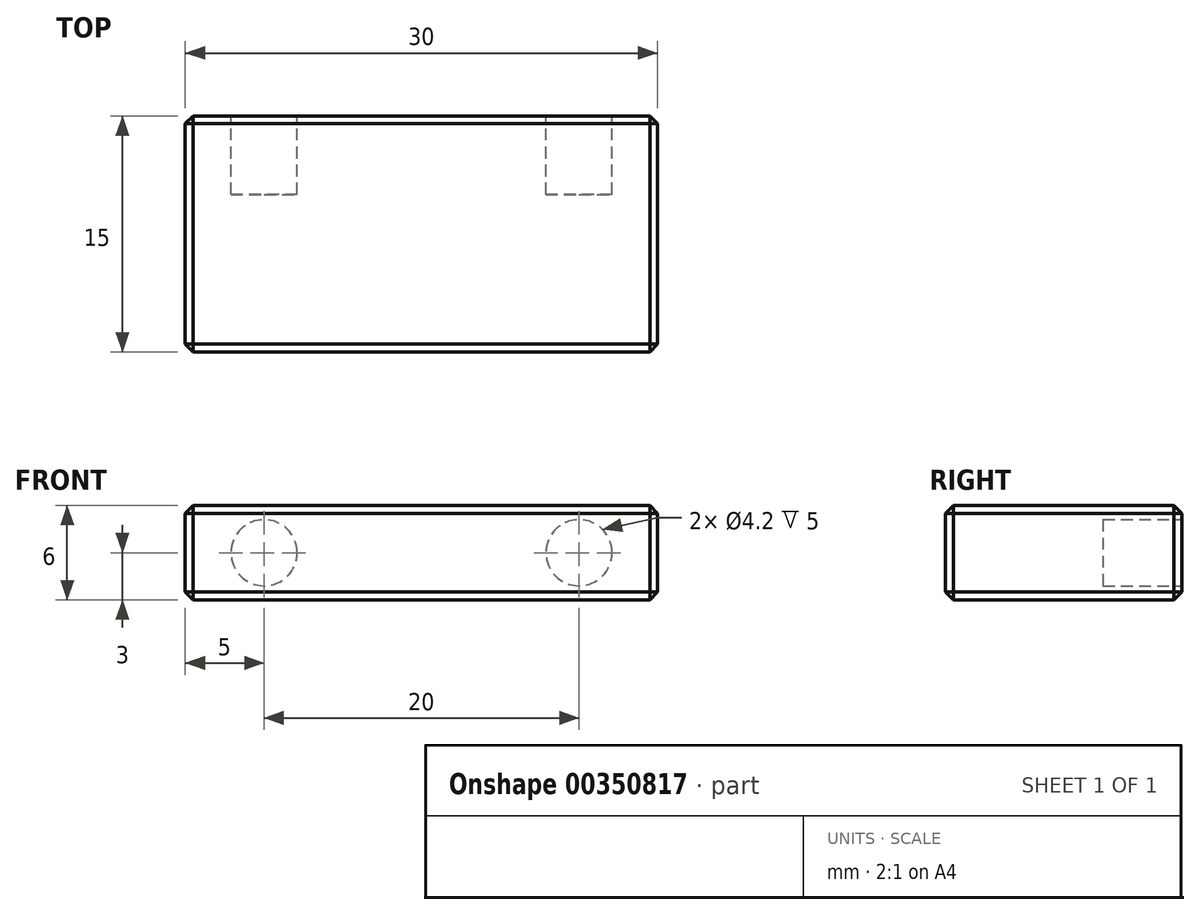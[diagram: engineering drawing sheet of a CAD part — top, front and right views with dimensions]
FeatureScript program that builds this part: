
annotation { "Feature Type Name" : "Feature", "Feature Type Description" : "" }
export const myFeature = defineFeature(function(context is Context, id is Id, definition is map)
    precondition{}
    {
        {
            var Q0;
            Q0=qCreatedBy(makeId("Front.planeOp"),FACE);
            var sketch = newSketch(context, id + "F0", { "sketchPlane" : qUnion([Q0])});
            skLineSegment(sketch, "E0.bottom", {"start": v(15, -3) * mm, "end": v(-15, -3) * mm});
            skLineSegment(sketch, "E0.top", {"start": v(15, 3) * mm, "end": v(-15, 3) * mm});
            skLineSegment(sketch, "E0.left", {"start": v(15, -3) * mm, "end": v(15, 3) * mm});
            skLineSegment(sketch, "E0.right", {"start": v(-15, -3) * mm, "end": v(-15, 3) * mm});
            skPoint(sketch, "E0.middle", {"position": v(0, 0) * mm});
            skSolve(sketch);
        }
        {
            var Q0;
            Q0 = qSketchRegion(id + "F0", true);
            extrude(context, id + "F1", {"entities" : qUnion([Q0]), "oppositeDirection" : true, "depth" : 15 * mm});
        }
        {
            var Q0;
            Q0=makeQuery(id+"F1.opExtrude","CAP_FACE",FACE,{"disambiguationData":[OSD([sQuery(id+"F0.wireOp",EDGE,"E0.bottom"),sQuery(id+"F0.wireOp",EDGE,"E0.top"),sQuery(id+"F0.wireOp",EDGE,"E0.left"),sQuery(id+"F0.wireOp",EDGE,"E0.right")])],"isStart":false});
            var sketch = newSketch(context, id + "F2", { "sketchPlane" : qUnion([Q0])});
            skCircle(sketch, "E1", {"center": v(-10, 0) * mm, "radius": 2.1 * mm});
            skCircle(sketch, "E2", {"center": v(10, 0) * mm, "radius": 2.1 * mm});
            skSolve(sketch);
        }
        {
            var Q0;
            Q0 = qSketchRegion(id + "F2", true);
            extrude(context, id + "F3", {"entities" : qUnion([Q0]), "operationType" : NewBodyOperationType.REMOVE, "oppositeDirection" : true, "depth" : 5 * mm});
        }
        {
            var Q0;
            Q0=makeQuery(id+"F1.opExtrude","SWEPT_FACE",FACE,{"disambiguationData":[OSD([sQuery(id+"F0.wireOp",EDGE,"E0.top")])]});
            var Q1;
            Q1=makeQuery(id+"F1.opExtrude","SWEPT_FACE",FACE,{"disambiguationData":[OSD([sQuery(id+"F0.wireOp",EDGE,"E0.bottom")])]});
            var Q2;
            Q2=makeQuery(id+"F1.opExtrude","SWEPT_FACE",FACE,{"disambiguationData":[OSD([sQuery(id+"F0.wireOp",EDGE,"E0.left")])]});
            var Q3;
            Q3=makeQuery(id+"F1.opExtrude","SWEPT_FACE",FACE,{"disambiguationData":[OSD([sQuery(id+"F0.wireOp",EDGE,"E0.right")])]});
            chamfer(context, id + "F4", {"entities" : qUnion([Q0, Q1, Q2, Q3]), "width" : .5 * mm, "tangentPropagation" : true});
        }
    });
